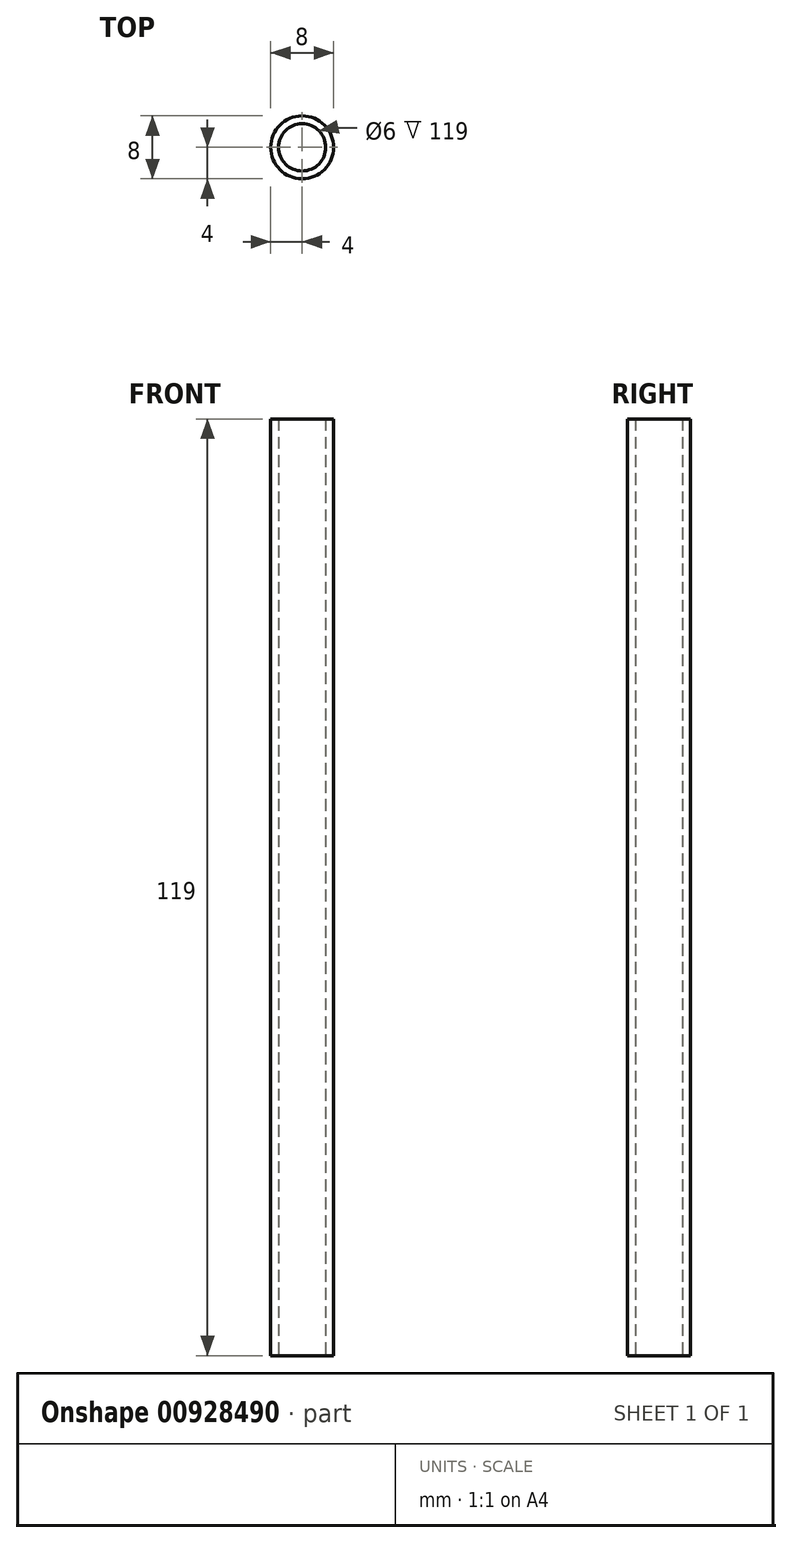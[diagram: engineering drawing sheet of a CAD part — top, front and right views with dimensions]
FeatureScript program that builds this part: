
annotation { "Feature Type Name" : "Feature", "Feature Type Description" : "" }
export const myFeature = defineFeature(function(context is Context, id is Id, definition is map)
    precondition{}
    {
        {
            var Q0;
            Q0=qCreatedBy(makeId("Top.planeOp"),FACE);
            var sketch = newSketch(context, id + "F0", { "sketchPlane" : qUnion([Q0])});
            skCircle(sketch, "E0", {"center": v(0, 0) * mm, "radius": 3 * mm});
            skCircle(sketch, "E1", {"center": v(0, 0) * mm, "radius": 4 * mm});
            skSolve(sketch);
        }
        {
            var Q0;
            Q0=makeQuery(id+"F0.imprint","IMPRINT",FACE,{"disambiguationData":[TD([[makeQuery(id+"F0.imprint","IMPRINT",EDGE,{"derivedFrom":sQuery(id+"F0.wireOp",EDGE,"E0")}),-1.0]])]});
            extrude(context, id + "F1", {"entities" : qUnion([Q0]), "depth" : 119 * mm, "offsetDistance" : 25 * mm});
        }
    });
